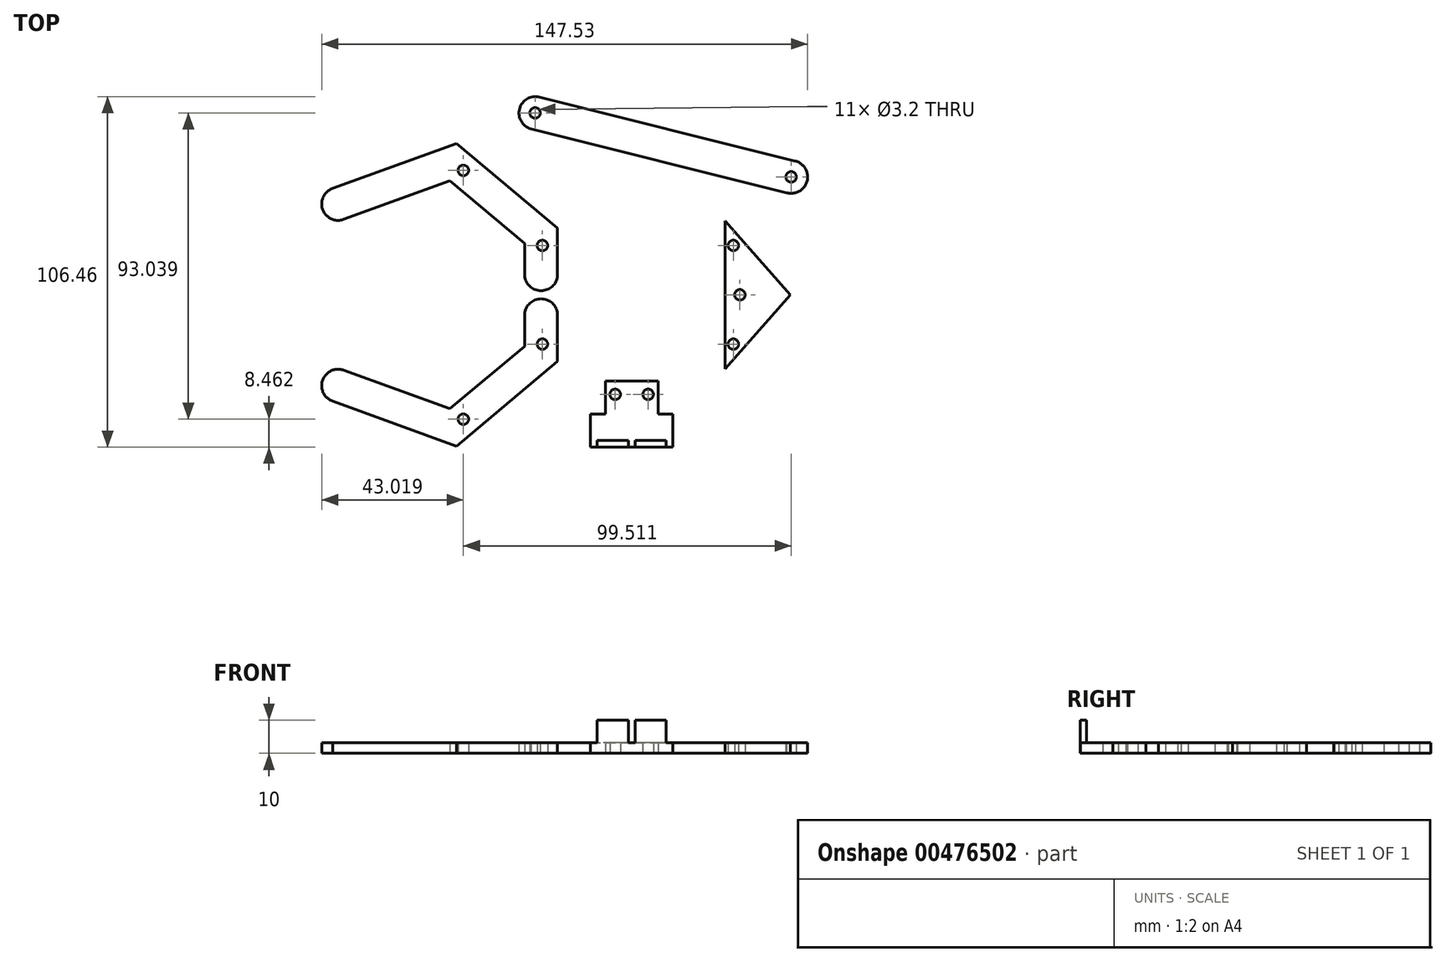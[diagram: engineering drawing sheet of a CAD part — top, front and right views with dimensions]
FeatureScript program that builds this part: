
annotation { "Feature Type Name" : "Feature", "Feature Type Description" : "" }
export const myFeature = defineFeature(function(context is Context, id is Id, definition is map)
    precondition{}
    {
        {
            var Q0;
            Q0=qCreatedBy(makeId("Top.planeOp"),FACE);
            var sketch = newSketch(context, id + "F0", { "sketchPlane" : qUnion([Q0])});
            skLineSegment(sketch, "E0", {"start": v(47.79, 22.5) * mm, "end": v(47.79, -22.5) * mm});
            skLineSegment(sketch, "E1", {"start": v(47.79, -22.5) * mm, "end": v(67.63, 0) * mm});
            skLineSegment(sketch, "E2", {"start": v(67.63, 0) * mm, "end": v(47.79, 22.5) * mm});
            skCircle(sketch, "E3", {"center": v(50.29, 15) * mm, "radius": 1.6 * mm});
            skCircle(sketch, "E4", {"center": v(50.29, -15) * mm, "radius": 1.6 * mm});
            skCircle(sketch, "E5", {"center": v(52.3, 0) * mm, "radius": 1.6 * mm});
            skSolve(sketch);
        }
        {
            var Q0;
            Q0 = qSketchRegion(id + "F0", true);
            extrude(context, id + "F1", {"entities" : qUnion([Q0]), "depth" : 3.2 * mm, "offsetDistance" : 25 * mm});
        }
        {
            var Q0;
            Q0=qCreatedBy(makeId("Top.planeOp"),FACE);
            var sketch = newSketch(context, id + "F2", { "sketchPlane" : qUnion([Q0])});
            skLineSegment(sketch, "E6", {"start": v(-3.1, 5.29) * mm, "end": v(-3.1, 20.29) * mm});
            skLineSegment(sketch, "E7", {"start": v(-13.1, 15.62) * mm, "end": v(-13.1, 6.3) * mm});
            skLineSegment(sketch, "E8", {"start": v(-3.1, 20.29) * mm, "end": v(-33.74, 46) * mm});
            skLineSegment(sketch, "E9", {"start": v(-13.1, 15.62) * mm, "end": v(-35.74, 34.63) * mm});
            skLineSegment(sketch, "E10", {"start": v(-33.74, 46) * mm, "end": v(-71.33, 32.32) * mm});
            skLineSegment(sketch, "E11", {"start": v(-35.74, 34.63) * mm, "end": v(-67.96, 22.9) * mm});
            skArc(sketch, "E12", {"start": v(-13.1, 6.3) * mm, "mid": v(-8.55, 1.27) * mm, "end": v(-3.1, 5.29) * mm});
            skArc(sketch, "E13", {"start": v(-67.96, 22.9) * mm, "mid": v(-74.38, 25.92) * mm, "end": v(-71.33, 32.32) * mm});
            skCircle(sketch, "E14", {"center": v(-7.65, 14.97) * mm, "radius": 1.6 * mm});
            skArc(sketch, "E15.MirrorCS", {"start": v(-13.1, -6.3) * mm, "mid": v(-8.55, -1.27) * mm, "end": v(-3.1, -5.29) * mm});
            skCircle(sketch, "E16.MirrorC", {"center": v(-7.65, -14.97) * mm, "radius": 1.6 * mm});
            skLineSegment(sketch, "E17.MirrorCS", {"start": v(-35.74, -34.63) * mm, "end": v(-67.96, -22.9) * mm});
            skArc(sketch, "E18.MirrorCS", {"start": v(-67.96, -22.9) * mm, "mid": v(-74.38, -25.92) * mm, "end": v(-71.33, -32.32) * mm});
            skLineSegment(sketch, "E19.MirrorCS", {"start": v(-33.74, -46) * mm, "end": v(-71.33, -32.32) * mm});
            skLineSegment(sketch, "E20.MirrorCS", {"start": v(-13.1, -15.62) * mm, "end": v(-35.74, -34.63) * mm});
            skLineSegment(sketch, "E21.MirrorCS", {"start": v(-3.1, -20.29) * mm, "end": v(-33.74, -46) * mm});
            skLineSegment(sketch, "E22.MirrorCS", {"start": v(-13.1, -15.62) * mm, "end": v(-13.1, -6.3) * mm});
            skLineSegment(sketch, "E23.MirrorCS", {"start": v(-3.1, -5.29) * mm, "end": v(-3.1, -20.29) * mm});
            skCircle(sketch, "E24", {"center": v(-31.66, 37.79) * mm, "radius": 1.6 * mm});
            skCircle(sketch, "E25.MirrorC", {"center": v(-31.66, -37.79) * mm, "radius": 1.6 * mm});
            skSolve(sketch);
        }
        {
            var Q0;
            Q0 = qSketchRegion(id + "F2", true);
            extrude(context, id + "F3", {"entities" : qUnion([Q0]), "depth" : 3.2 * mm, "offsetDistance" : 25 * mm});
        }
        {
            var Q0;
            Q0=qCreatedBy(makeId("Top.planeOp"),FACE);
            var sketch = newSketch(context, id + "F4", { "sketchPlane" : qUnion([Q0])});
            skLineSegment(sketch, "E26", {"start": v(-11.12, 50.4) * mm, "end": v(66.5, 31) * mm});
            skLineSegment(sketch, "E27", {"start": v(-8.55, 60.07) * mm, "end": v(69.06, 40.67) * mm});
            skCircle(sketch, "E28", {"center": v(-9.9, 55.25) * mm, "radius": 1.6 * mm});
            skCircle(sketch, "E29", {"center": v(67.85, 35.81) * mm, "radius": 1.6 * mm});
            skArc(sketch, "E30", {"start": v(-8.55, 60.07) * mm, "mid": v(-14.6, 56.5) * mm, "end": v(-11.12, 50.4) * mm});
            skArc(sketch, "E31", {"start": v(69.06, 40.67) * mm, "mid": v(72.68, 34.53) * mm, "end": v(66.5, 31) * mm});
            skSolve(sketch);
        }
        {
            var Q0;
            Q0=makeQuery(id+"F4.imprint","IMPRINT",FACE,{"disambiguationData":[TD([[makeQuery(id+"F4.imprint","IMPRINT",EDGE,{"derivedFrom":sQuery(id+"F4.wireOp",EDGE,"E26")}),1.0]])]});
            extrude(context, id + "F5", {"entities" : qUnion([Q0]), "depth" : 3.2 * mm, "offsetDistance" : 25 * mm});
        }
        {
            var Q0;
            Q0=qCreatedBy(makeId("Top.planeOp"),FACE);
            var sketch = newSketch(context, id + "F6", { "sketchPlane" : qUnion([Q0])});
            skLineSegment(sketch, "E32.bottom", {"start": v(27.43, -36.25) * mm, "end": v(11.43, -36.25) * mm});
            skLineSegment(sketch, "E32.top", {"start": v(27.43, -26.25) * mm, "end": v(11.43, -26.25) * mm});
            skLineSegment(sketch, "E32.left", {"start": v(27.43, -36.25) * mm, "end": v(27.43, -26.25) * mm});
            skLineSegment(sketch, "E32.right", {"start": v(11.43, -36.25) * mm, "end": v(11.43, -26.25) * mm});
            skPoint(sketch, "E32.middle", {"position": v(19.43, -31.25) * mm});
            skCircle(sketch, "E33", {"center": v(14.43, -30.25) * mm, "radius": 1.6 * mm});
            skCircle(sketch, "E34", {"center": v(24.43, -30.25) * mm, "radius": 1.6 * mm});
            skLineSegment(sketch, "E35.bottom", {"start": v(6.93, -46.25) * mm, "end": v(31.93, -46.25) * mm});
            skLineSegment(sketch, "E35.top", {"start": v(6.93, -36.25) * mm, "end": v(31.93, -36.25) * mm});
            skLineSegment(sketch, "E35.left", {"start": v(6.93, -46.25) * mm, "end": v(6.93, -36.25) * mm});
            skLineSegment(sketch, "E35.right", {"start": v(31.93, -46.25) * mm, "end": v(31.93, -36.25) * mm});
            skPoint(sketch, "E35.middle", {"position": v(19.43, -41.25) * mm});
            skLineSegment(sketch, "E36.bottom", {"start": v(6.93, -46.25) * mm, "end": v(11.43, -46.25) * mm});
            skLineSegment(sketch, "E36.top", {"start": v(6.93, -36.25) * mm, "end": v(11.43, -36.25) * mm});
            skLineSegment(sketch, "E36.right", {"start": v(11.43, -46.25) * mm, "end": v(11.43, -36.25) * mm, "construction": true});
            skLineSegment(sketch, "E37.bottom", {"start": v(31.93, -46.25) * mm, "end": v(27.43, -46.25) * mm});
            skLineSegment(sketch, "E37.top", {"start": v(31.93, -36.25) * mm, "end": v(27.43, -36.25) * mm});
            skLineSegment(sketch, "E37.right", {"start": v(27.43, -46.25) * mm, "end": v(27.43, -36.25) * mm, "construction": true});
            skPoint(sketch, "E38", {"position": v(31.93, -38.25) * mm});
            skLineSegment(sketch, "E39.bottom", {"start": v(31.93, -38.25) * mm, "end": v(6.93, -38.25) * mm});
            skLineSegment(sketch, "E39.top", {"start": v(31.93, -36.25) * mm, "end": v(6.93, -36.25) * mm});
            skLineSegment(sketch, "E39.left", {"start": v(31.93, -38.25) * mm, "end": v(31.93, -36.25) * mm});
            skLineSegment(sketch, "E39.right", {"start": v(6.93, -38.25) * mm, "end": v(6.93, -36.25) * mm});
            skPoint(sketch, "E40", {"position": v(31.93, -44.25) * mm});
            skPoint(sketch, "E41", {"position": v(6.93, -44.25) * mm});
            skPoint(sketch, "E42", {"position": v(18.43, -44.25) * mm});
            skPoint(sketch, "E43", {"position": v(20.43, -44.25) * mm});
            skLineSegment(sketch, "E44.bottom", {"start": v(20.43, -44.25) * mm, "end": v(31.93, -44.25) * mm});
            skLineSegment(sketch, "E44.top", {"start": v(20.43, -46.25) * mm, "end": v(31.93, -46.25) * mm});
            skLineSegment(sketch, "E44.left", {"start": v(20.43, -44.25) * mm, "end": v(20.43, -46.25) * mm});
            skLineSegment(sketch, "E44.right", {"start": v(31.93, -44.25) * mm, "end": v(31.93, -46.25) * mm});
            skLineSegment(sketch, "E45.bottom", {"start": v(6.93, -46.25) * mm, "end": v(18.43, -46.25) * mm});
            skLineSegment(sketch, "E45.top", {"start": v(6.93, -44.25) * mm, "end": v(18.43, -44.25) * mm});
            skLineSegment(sketch, "E45.left", {"start": v(6.93, -46.25) * mm, "end": v(6.93, -44.25) * mm});
            skLineSegment(sketch, "E45.right", {"start": v(18.43, -46.25) * mm, "end": v(18.43, -44.25) * mm});
            skPoint(sketch, "E46", {"position": v(8.93, -36.25) * mm});
            skPoint(sketch, "E47", {"position": v(29.93, -36.25) * mm});
            skLineSegment(sketch, "E48.bottom", {"start": v(31.93, -46.25) * mm, "end": v(29.93, -46.25) * mm});
            skLineSegment(sketch, "E48.top", {"start": v(31.93, -36.25) * mm, "end": v(29.93, -36.25) * mm});
            skLineSegment(sketch, "E48.right", {"start": v(29.93, -46.25) * mm, "end": v(29.93, -36.25) * mm});
            skLineSegment(sketch, "E49.bottom", {"start": v(6.93, -46.25) * mm, "end": v(8.93, -46.25) * mm});
            skLineSegment(sketch, "E49.top", {"start": v(6.93, -36.25) * mm, "end": v(8.93, -36.25) * mm});
            skLineSegment(sketch, "E49.right", {"start": v(8.93, -46.25) * mm, "end": v(8.93, -36.25) * mm});
            skSolve(sketch);
        }
        {
            var Q0;
            Q0 = qSketchRegion(id + "F6", true);
            extrude(context, id + "F7", {"entities" : qUnion([Q0]), "depth" : 3.2 * mm, "offsetDistance" : 25 * mm});
        }
        {
            var Q0;
            {var subQ0=sQuery(id+"F6.wireOp",EDGE,"E45.right");Q0=makeQuery(id+"F6.imprint","IMPRINT",FACE,{"disambiguationData":[TD([[makeQuery(id+"F6.imprint","IMPRINT",EDGE,{"derivedFrom":subQ0}),1.0]])]});}
            var Q1;
            {var subQ0=sQuery(id+"F6.wireOp",EDGE,"E44.left");Q1=makeQuery(id+"F6.imprint","IMPRINT",FACE,{"disambiguationData":[TD([[makeQuery(id+"F6.imprint","IMPRINT",EDGE,{"derivedFrom":subQ0}),1.0]])]});}
            extrude(context, id + "F9", {"entities" : qUnion([Q0, Q1]), "operationType" : NewBodyOperationType.ADD, "depth" : 10 * mm, "offsetDistance" : 25 * mm});
        }
    });
